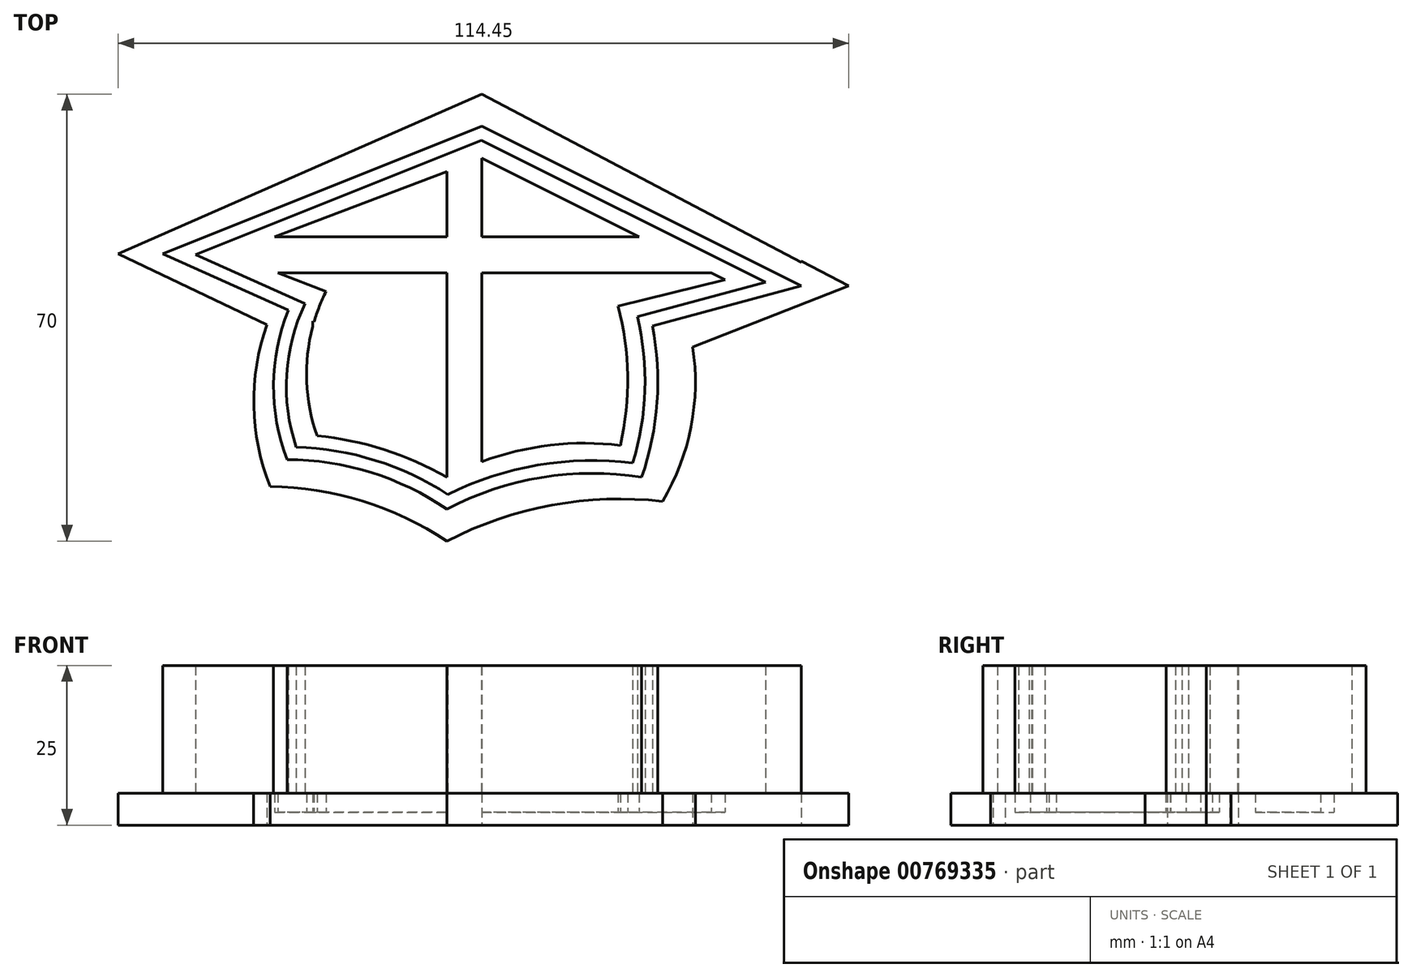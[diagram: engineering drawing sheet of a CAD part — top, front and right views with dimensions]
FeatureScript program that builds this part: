
annotation { "Feature Type Name" : "Feature", "Feature Type Description" : "" }
export const myFeature = defineFeature(function(context is Context, id is Id, definition is map)
    precondition{}
    {
        {
            var Q0;
            Q0=qCreatedBy(makeId("Top.planeOp"),FACE);
            var sketch = newSketch(context, id + "F0", { "sketchPlane" : qUnion([Q0])});
            skLineSegment(sketch, "E0.bottom", {"start": v(50, 50) * mm, "end": v(-50, 50) * mm});
            skLineSegment(sketch, "E0.top", {"start": v(50, -50) * mm, "end": v(-50, -50) * mm});
            skLineSegment(sketch, "E0.left", {"start": v(50, 50) * mm, "end": v(50, -50) * mm});
            skLineSegment(sketch, "E0.right", {"start": v(-50, 50) * mm, "end": v(-50, -50) * mm});
            skPoint(sketch, "E0.middle", {"position": v(0, 0) * mm});
            skLineSegment(sketch, "E1", {"start": v(0, 32.68) * mm, "end": v(0, 30) * mm});
            skLineSegment(sketch, "E2", {"start": v(0, 45) * mm, "end": v(0, 25) * mm});
            skLineSegment(sketch, "E3", {"start": v(35, 25) * mm, "end": v(34.13, 25) * mm});
            skLineSegment(sketch, "E4", {"start": v(0, -10) * mm, "end": v(-5.5, -10) * mm});
            skLineSegment(sketch, "E5", {"start": v(-5.5, -10) * mm, "end": v(-5.5, -5) * mm});
            skArc(sketch, "E6", {"start": v(25, -5) * mm, "mid": v(9.34, -5.03) * mm, "end": v(-5.5, -10) * mm});
            skArc(sketch, "E7", {"start": v(25, -5) * mm, "mid": v(27.54, 10) * mm, "end": v(25, 25) * mm});
            skLineSegment(sketch, "E8", {"start": v(0, 45) * mm, "end": v(0, 10) * mm});
            skLineSegment(sketch, "E9", {"start": v(-50, 30) * mm, "end": v(0, 50) * mm});
            skLineSegment(sketch, "E10", {"start": v(50, 25) * mm, "end": v(0, 50) * mm});
            skLineSegment(sketch, "E11", {"start": v(0, 45) * mm, "end": v(0, 32.68) * mm});
            skLineSegment(sketch, "E12", {"start": v(-50, 30) * mm, "end": v(-30.35, 21.17) * mm});
            skLineSegment(sketch, "E13", {"start": v(50, 25) * mm, "end": v(22.23, 17.5) * mm});
            skLineSegment(sketch, "E14", {"start": v(-5.5, -10) * mm, "end": v(-5.5, -2.25) * mm});
            skPoint(sketch, "E14.endSnap0", {"position": v(-5.5, -7.5) * mm});
            skLineSegment(sketch, "E15", {"start": v(-5.5, -2.25) * mm, "end": v(-30.5, -2.25) * mm});
            skLineSegment(sketch, "E16", {"start": v(-30.5, -2.25) * mm, "end": v(-26.5, -2.25) * mm});
            skLineSegment(sketch, "E17", {"start": v(-26.5, -2.25) * mm, "end": v(-26.5, 3.69) * mm});
            skArc(sketch, "E18", {"start": v(-5.5, -10) * mm, "mid": v(-17.41, -4.23) * mm, "end": v(-30.5, -2.25) * mm});
            skArc(sketch, "E19", {"start": v(-30.35, 21.17) * mm, "mid": v(-32.65, 9.47) * mm, "end": v(-30.5, -2.25) * mm});
            skLineSegment(sketch, "E20", {"start": v(35, 20.95) * mm, "end": v(35.5, 20.95) * mm});
            skLineSegment(sketch, "E21", {"start": v(0, 55) * mm, "end": v(57, 25) * mm});
            skLineSegment(sketch, "E22", {"start": v(-57, 30) * mm, "end": v(0, 55) * mm});
            skLineSegment(sketch, "E23", {"start": v(-57, 30) * mm, "end": v(-33.7, 18.9) * mm});
            skArc(sketch, "E24", {"start": v(-33.7, 18.9) * mm, "mid": v(-35.75, 6.17) * mm, "end": v(-33.19, -6.47) * mm});
            skLineSegment(sketch, "E25", {"start": v(-5.5, -10) * mm, "end": v(-5.5, -15) * mm});
            skArc(sketch, "E26", {"start": v(-5.5, -15) * mm, "mid": v(-18.72, -8.73) * mm, "end": v(-33.19, -6.47) * mm});
            skLineSegment(sketch, "E27", {"start": v(33.01, 15.41) * mm, "end": v(57.45, 25) * mm});
            skArc(sketch, "E28", {"start": v(28.28, -8.77) * mm, "mid": v(32.74, 2.91) * mm, "end": v(33.01, 15.41) * mm});
            skArc(sketch, "E29", {"start": v(28.28, -8.77) * mm, "mid": v(10.93, -9.38) * mm, "end": v(-5.5, -15) * mm});
            skLineSegment(sketch, "E30", {"start": v(0, 45) * mm, "end": v(-39.53, 30) * mm});
            skLineSegment(sketch, "E31", {"start": v(-39.53, 30) * mm, "end": v(-24.42, 24.1) * mm});
            skLineSegment(sketch, "E32", {"start": v(0, 45) * mm, "end": v(38.06, 25.97) * mm});
            skLineSegment(sketch, "E33", {"start": v(38.06, 25.97) * mm, "end": v(21.32, 21.84) * mm});
            skArc(sketch, "E34", {"start": v(-24.42, 24.1) * mm, "mid": v(-27.43, 12.95) * mm, "end": v(-25.83, 1.51) * mm});
            skArc(sketch, "E35", {"start": v(-5.5, -5) * mm, "mid": v(-15.32, -0.68) * mm, "end": v(-25.83, 1.51) * mm});
            skArc(sketch, "E36", {"start": v(21.68, 0) * mm, "mid": v(7.7, -0.42) * mm, "end": v(-5.5, -5) * mm});
            skArc(sketch, "E37", {"start": v(21.68, 0) * mm, "mid": v(22.8, 10.94) * mm, "end": v(21.32, 21.84) * mm});
            skLineSegment(sketch, "E38", {"start": v(-5.5, -5) * mm, "end": v(-5.5, 27.05) * mm});
            skPoint(sketch, "E39.endSnap0", {"position": v(2, -5) * mm});
            skLineSegment(sketch, "E40", {"start": v(-31.97, 27.05) * mm, "end": v(-5.5, 27.05) * mm});
            skLineSegment(sketch, "E41", {"start": v(35.9, 27.05) * mm, "end": v(24.64, 32.68) * mm});
            skLineSegment(sketch, "E42", {"start": v(24.64, 32.68) * mm, "end": v(0, 32.68) * mm});
            skLineSegment(sketch, "E43.trimOffspring", {"start": v(34.13, 25) * mm, "end": v(35, 25) * mm});
            skPoint(sketch, "E44.orphan", {"position": v(-37.04, 16.62) * mm});
            skPoint(sketch, "E45.orphan", {"position": v(2, 44) * mm});
            skPoint(sketch, "E46.trimOffspring.end.orphan", {"position": v(9.5, -5) * mm});
            skPoint(sketch, "E47.orphan", {"position": v(-30.35, 15) * mm});
            skLineSegment(sketch, "E48.trimOffspring", {"start": v(-26.5, 18.63) * mm, "end": v(-26.5, 19.44) * mm});
            skLineSegment(sketch, "E49.trimOffspring", {"start": v(-26.5, 19.44) * mm, "end": v(-26.3, 19.35) * mm});
            skLineSegment(sketch, "E50.trimOffspring", {"start": v(-5.5, 32.68) * mm, "end": v(-5.5, 42.91) * mm});
            skLineSegment(sketch, "E51.trimOffspring", {"start": v(-5.5, 32.68) * mm, "end": v(-32.46, 32.68) * mm});
            skLineSegment(sketch, "E52.trimOffspring", {"start": v(0, 27.05) * mm, "end": v(35.9, 27.05) * mm});
            skLineSegment(sketch, "E53.trimOffspring", {"start": v(0, 30) * mm, "end": v(0, 15) * mm});
            skLineSegment(sketch, "E54.trimOffspring", {"start": v(0, 30) * mm, "end": v(0, 10) * mm});
            skLineSegment(sketch, "E55", {"start": v(0, 10) * mm, "end": v(0, -2.54) * mm});
            skLineSegment(sketch, "E56", {"start": v(26.7, 18.7) * mm, "end": v(50, 25) * mm});
            skLineSegment(sketch, "E57", {"start": v(0, 55) * mm, "end": v(57.45, 25) * mm});
            skSolve(sketch);
        }
        {
            var Q0;
            Q0=makeQuery(id+"F0.imprint","IMPRINT",FACE,{"disambiguationData":[TD([[makeQuery(id+"F0.imprint","IMPRINT",EDGE,{"derivedFrom":sQuery(id+"F0.wireOp",EDGE,"E9")}),-1.0]])]});
            var Q1;
            {var subQ3=sQuery(id+"F0.wireOp",EDGE,"E17");Q1=makeQuery(id+"F0.imprint","IMPRINT",FACE,{"disambiguationData":[TD([[makeQuery(id+"F0.imprint","IMPRINT",EDGE,{"derivedFrom":subQ3}),-1.0]])]});}
            var Q2;
            {var subQ6=sQuery(id+"F0.wireOp",EDGE,"E5");Q2=makeQuery(id+"F0.imprint","IMPRINT",FACE,{"disambiguationData":[TD([[makeQuery(id+"F0.imprint","IMPRINT",EDGE,{"derivedFrom":subQ6}),-1.0]])]});}
            var Q3;
            {var subQ5=sQuery(id+"F0.wireOp",EDGE,"E5");Q3=makeQuery(id+"F0.imprint","IMPRINT",FACE,{"disambiguationData":[TD([[makeQuery(id+"F0.imprint","IMPRINT",EDGE,{"derivedFrom":subQ5}),1.0]])]});}
            var Q4;
            {var subQ0=sQuery(id+"F0.wireOp",EDGE,"E14");Q4=makeQuery(id+"F0.imprint","IMPRINT",FACE,{"disambiguationData":[TD([[makeQuery(id+"F0.imprint","IMPRINT",EDGE,{"derivedFrom":subQ0}),1.0]])]});}
            var Q5;
            {var subQ14=sQuery(id+"F0.wireOp",EDGE,"E1");Q5=makeQuery(id+"F0.imprint","IMPRINT",FACE,{"disambiguationData":[TD([[makeQuery(id+"F0.imprint","IMPRINT",EDGE,{"derivedFrom":subQ14}),-1.0]])]});}
            var Q6;
            {var subQ15=sQuery(id+"F0.wireOp",EDGE,"E52.trimOffspring");Q6=makeQuery(id+"F0.imprint","IMPRINT",FACE,{"disambiguationData":[TD([[makeQuery(id+"F0.imprint","IMPRINT",EDGE,{"derivedFrom":subQ15}),-1.0]])]});}
            var Q7;
            {var subQ0=sQuery(id+"F0.wireOp",EDGE,"E13");var subQ1=sQuery(id+"F0.wireOp",EDGE,"E7");var subQ2=makeQuery(id+"F0.imprint","INTERSECT",VERTEX,{"derivedFrom":[subQ1,subQ0]});Q7=makeQuery(id+"F0.imprint","IMPRINT",FACE,{"disambiguationData":[TD([[makeQuery(id+"F0.imprint","IMPRINT",EDGE,{"disambiguationData":[TD([[subQ2,-1.0]])],"derivedFrom":subQ1}),1.0]])]});}
            var Q8;
            {var subQ4=sQuery(id+"F0.wireOp",EDGE,"E1");Q8=makeQuery(id+"F0.imprint","IMPRINT",FACE,{"disambiguationData":[TD([[makeQuery(id+"F0.imprint","IMPRINT",EDGE,{"derivedFrom":subQ4}),1.0]])]});}
            var Q9;
            {var subQ0=sQuery(id+"F0.wireOp",EDGE,"E42");Q9=makeQuery(id+"F0.imprint","IMPRINT",FACE,{"disambiguationData":[TD([[makeQuery(id+"F0.imprint","IMPRINT",EDGE,{"derivedFrom":subQ0}),-1.0]])]});}
            var Q10;
            {var subQ0=sQuery(id+"F0.wireOp",EDGE,"E50.trimOffspring");Q10=makeQuery(id+"F0.imprint","IMPRINT",FACE,{"disambiguationData":[TD([[makeQuery(id+"F0.imprint","IMPRINT",EDGE,{"derivedFrom":subQ0}),1.0]])]});}
            var Q11;
            {var subQ6=sQuery(id+"F0.wireOp",EDGE,"E38");Q11=makeQuery(id+"F0.imprint","IMPRINT",FACE,{"disambiguationData":[TD([[makeQuery(id+"F0.imprint","IMPRINT",EDGE,{"derivedFrom":subQ6}),1.0]])]});}
            var Q12;
            {var subQ0=sQuery(id+"F0.wireOp",EDGE,"E48.trimOffspring");Q12=makeQuery(id+"F0.imprint","IMPRINT",FACE,{"disambiguationData":[TD([[makeQuery(id+"F0.imprint","IMPRINT",EDGE,{"derivedFrom":subQ0}),-1.0]])]});}
            extrude(context, id + "F1", {"entities" : qUnion([Q0, Q1, Q2, Q3, Q4, Q5, Q6, Q7, Q8, Q9, Q10, Q11, Q12]), "depth" : 25 * mm, "offsetDistance" : 25 * mm});
        }
        {
            var Q0;
            Q0=makeQuery(id+"F1.opExtrude","CAP_FACE",FACE,{"disambiguationData":[OSD([sQuery(id+"F0.wireOp",EDGE,"E6"),sQuery(id+"F0.wireOp",EDGE,"E7"),sQuery(id+"F0.wireOp",EDGE,"E9"),sQuery(id+"F0.wireOp",EDGE,"E10"),sQuery(id+"F0.wireOp",EDGE,"E12"),sQuery(id+"F0.wireOp",EDGE,"E13"),sQuery(id+"F0.wireOp",EDGE,"E18"),sQuery(id+"F0.wireOp",EDGE,"E19")])],"isStart":false});
            shell(context, id + "F2", {"entities" : qUnion([Q0]), "thickness" : 2 * mm});
        }
        {
            var Q0;
            {var subQ6=sQuery(id+"F0.wireOp",EDGE,"E6");Q0=makeQuery(id+"F0.imprint","IMPRINT",FACE,{"disambiguationData":[TD([[makeQuery(id+"F0.imprint","IMPRINT",EDGE,{"derivedFrom":subQ6}),1.0]])]});}
            var Q1;
            {var subQ3=sQuery(id+"F0.wireOp",EDGE,"E10");Q1=makeQuery(id+"F0.imprint","IMPRINT",FACE,{"disambiguationData":[TD([[makeQuery(id+"F0.imprint","IMPRINT",EDGE,{"derivedFrom":subQ3}),-1.0]])]});}
            var Q2;
            {var subQ0=sQuery(id+"F0.wireOp",EDGE,"E0.bottom");var subQ2=sQuery(id+"F0.wireOp",EDGE,"E22");var subQ3=makeQuery(id+"F0.imprint","INTERSECT",VERTEX,{"derivedFrom":[subQ0,subQ2]});Q2=makeQuery(id+"F0.imprint","IMPRINT",FACE,{"disambiguationData":[TD([[makeQuery(id+"F0.imprint","IMPRINT",EDGE,{"disambiguationData":[TD([[subQ3,1.0]])],"derivedFrom":subQ0}),-1.0]])]});}
            var Q3;
            {var subQ0=sQuery(id+"F0.wireOp",EDGE,"E9");Q3=makeQuery(id+"F0.imprint","IMPRINT",FACE,{"disambiguationData":[TD([[makeQuery(id+"F0.imprint","IMPRINT",EDGE,{"derivedFrom":subQ0}),1.0]])]});}
            var Q4;
            {var subQ1=sQuery(id+"F0.wireOp",EDGE,"E0.right");var subQ4=sQuery(id+"F0.wireOp",EDGE,"E22");var subQ5=makeQuery(id+"F0.imprint","INTERSECT",VERTEX,{"derivedFrom":[subQ1,subQ4]});Q4=makeQuery(id+"F0.imprint","IMPRINT",FACE,{"disambiguationData":[TD([[makeQuery(id+"F0.imprint","IMPRINT",EDGE,{"disambiguationData":[TD([[subQ5,1.0]])],"derivedFrom":subQ4}),-1.0]])]});}
            var Q5;
            {var subQ0=sQuery(id+"F0.wireOp",EDGE,"E12");Q5=makeQuery(id+"F0.imprint","IMPRINT",FACE,{"disambiguationData":[TD([[makeQuery(id+"F0.imprint","IMPRINT",EDGE,{"derivedFrom":subQ0}),-1.0]])]});}
            var Q6;
            {var subQ6=sQuery(id+"F0.wireOp",EDGE,"E5");Q6=makeQuery(id+"F0.imprint","IMPRINT",FACE,{"disambiguationData":[TD([[makeQuery(id+"F0.imprint","IMPRINT",EDGE,{"derivedFrom":subQ6}),-1.0]])]});}
            var Q7;
            {var subQ5=sQuery(id+"F0.wireOp",EDGE,"E5");Q7=makeQuery(id+"F0.imprint","IMPRINT",FACE,{"disambiguationData":[TD([[makeQuery(id+"F0.imprint","IMPRINT",EDGE,{"derivedFrom":subQ5}),1.0]])]});}
            var Q8;
            {var subQ3=sQuery(id+"F0.wireOp",EDGE,"E17");Q8=makeQuery(id+"F0.imprint","IMPRINT",FACE,{"disambiguationData":[TD([[makeQuery(id+"F0.imprint","IMPRINT",EDGE,{"derivedFrom":subQ3}),-1.0]])]});}
            var Q9;
            Q9=makeQuery(id+"F0.imprint","IMPRINT",FACE,{"disambiguationData":[TD([[makeQuery(id+"F0.imprint","IMPRINT",EDGE,{"derivedFrom":sQuery(id+"F0.wireOp",EDGE,"E9")}),-1.0]])]});
            var Q10;
            {var subQ0=sQuery(id+"F0.wireOp",EDGE,"E13");var subQ1=sQuery(id+"F0.wireOp",EDGE,"E7");var subQ2=makeQuery(id+"F0.imprint","INTERSECT",VERTEX,{"derivedFrom":[subQ1,subQ0]});Q10=makeQuery(id+"F0.imprint","IMPRINT",FACE,{"disambiguationData":[TD([[makeQuery(id+"F0.imprint","IMPRINT",EDGE,{"disambiguationData":[TD([[subQ2,-1.0]])],"derivedFrom":subQ1}),1.0]])]});}
            var Q11;
            {var subQ14=sQuery(id+"F0.wireOp",EDGE,"E1");Q11=makeQuery(id+"F0.imprint","IMPRINT",FACE,{"disambiguationData":[TD([[makeQuery(id+"F0.imprint","IMPRINT",EDGE,{"derivedFrom":subQ14}),-1.0]])]});}
            var Q12;
            {var subQ4=sQuery(id+"F0.wireOp",EDGE,"E1");Q12=makeQuery(id+"F0.imprint","IMPRINT",FACE,{"disambiguationData":[TD([[makeQuery(id+"F0.imprint","IMPRINT",EDGE,{"derivedFrom":subQ4}),1.0]])]});}
            var Q13;
            {var subQ0=sQuery(id+"F0.wireOp",EDGE,"E0.left");var subQ1=makeQuery(id+"F0.imprint","INTERSECT",VERTEX,{"derivedFrom":[subQ0,sQuery(id+"F0.wireOp",EDGE,"E21")]});Q13=makeQuery(id+"F0.imprint","IMPRINT",FACE,{"disambiguationData":[TD([[makeQuery(id+"F0.imprint","IMPRINT",EDGE,{"disambiguationData":[TD([[subQ1,1.0]])],"derivedFrom":subQ0}),1.0]])]});}
            extrude(context, id + "F3", {"entities" : qUnion([Q0, Q1, Q2, Q3, Q4, Q5, Q6, Q7, Q8, Q9, Q10, Q11, Q12, Q13]), "operationType" : NewBodyOperationType.ADD, "depth" : 5 * mm, "offsetDistance" : 25 * mm});
        }
    });
